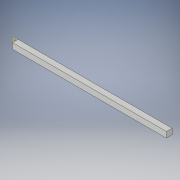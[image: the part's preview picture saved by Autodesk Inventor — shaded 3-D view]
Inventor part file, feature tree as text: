
AUTODESK INVENTOR PART (.ipt)
format: ipt  version: 2017 (Build 210142000, 142)  size: 92,672 bytes
history: native  units: in
note: dims shown in document units (in); Inventor stores cm internally (conversion verified against a paired STEP export)
features: plane x1, extrude x1, sketch x1
ambient origin geometry x8: Origin, YZ Plane, XZ Plane, XY Plane, X Axis, Y Axis, Z Axis, Center Point
bodies: Solid1 (feature_tree)
feature tree (3):
  plane  "Work Plane1"
  extrude  "Extrusion1"  Depth=13.5in
  sketch  "Sketch1"  dims[d0=0.125in d1=13.5in d2=0.5in d3=0.5in d4=0.0in]
